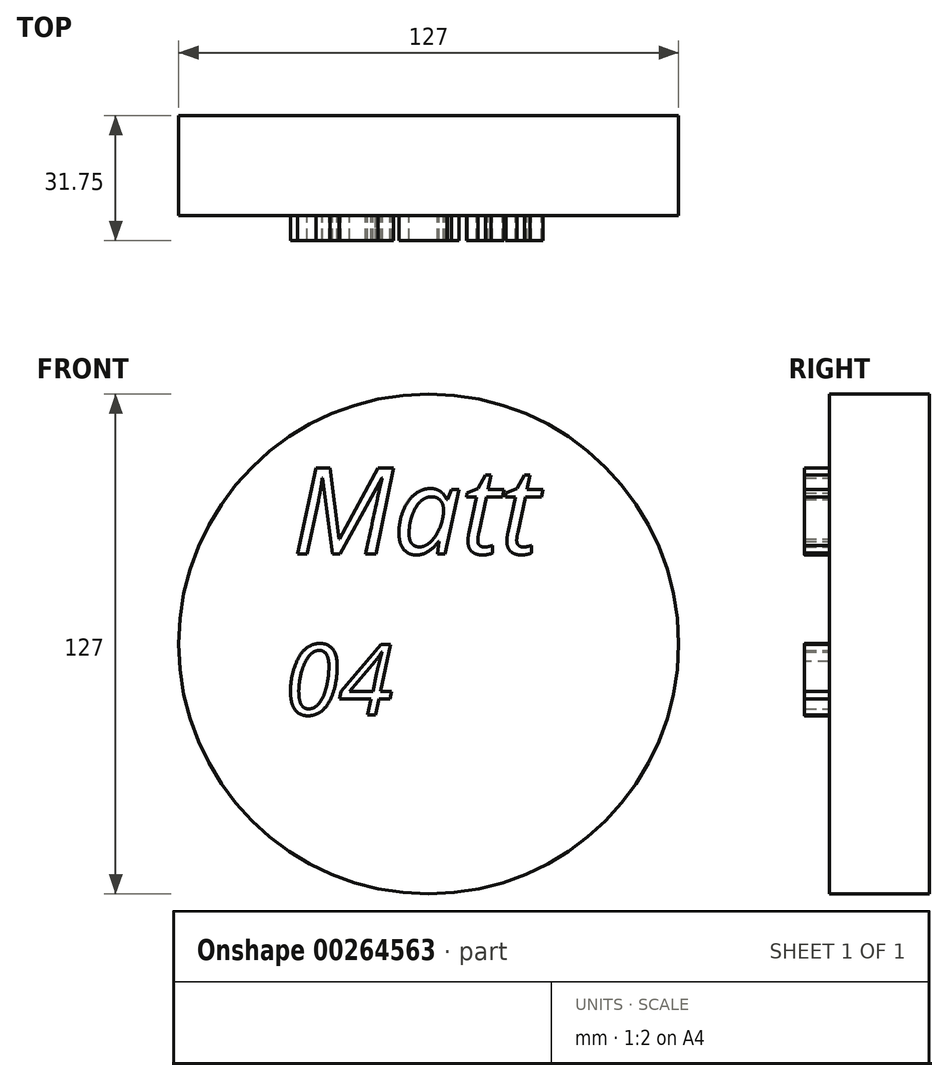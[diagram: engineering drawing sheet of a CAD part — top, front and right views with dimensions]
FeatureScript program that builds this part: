
annotation { "Feature Type Name" : "Feature", "Feature Type Description" : "" }
export const myFeature = defineFeature(function(context is Context, id is Id, definition is map)
    precondition{}
    {
        {
            var Q0;
            Q0=qCreatedBy(makeId("Front.planeOp"),FACE);
            var sketch = newSketch(context, id + "F0", { "sketchPlane" : qUnion([Q0])});
            skCircle(sketch, "E0", {"center": v(0, 0) * mm, "radius": 63.5 * mm});
            skSolve(sketch);
        }
        {
            var Q0;
            Q0=makeQuery(id+"F0.imprint","IMPRINT",FACE,{"disambiguationData":[TD([[makeQuery(id+"F0.imprint","IMPRINT",EDGE,{"derivedFrom":sQuery(id+"F0.wireOp",EDGE,"E0")}),1.0]])]});
            extrude(context, id + "F1", {"entities" : qUnion([Q0]), "depth" : 25.4 * mm});
        }
        {
            var Q0;
            Q0=makeQuery(id+"F1.opExtrude","CAP_FACE",FACE,{"disambiguationData":[OSD([sQuery(id+"F0.wireOp",EDGE,"E0")])],"isStart":false});
            var sketch = newSketch(context, id + "F2", { "sketchPlane" : qUnion([Q0])});
            skText(sketch, "E1", { "text": "Matt", "fontName": "OpenSans-Italic.ttf"});
            skText(sketch, "E2", { "text": "04", "fontName": "OpenSans-Italic.ttf"});
            const initialGuessF2  = {"E1": [-0.03452, 0.02289, 1, 0, 0.02196], "E2": [-0.03657, -0.018, 1, 0, 0.018]};
            skSetInitialGuess(sketch, initialGuessF2);
            skSolve(sketch);
        }
        {
            var Q0;
            Q0 = qSketchRegion(id + "F2", true);
            extrude(context, id + "F3", {"entities" : qUnion([Q0]), "operationType" : NewBodyOperationType.ADD, "depth" : 6.35 * mm});
        }
    });
